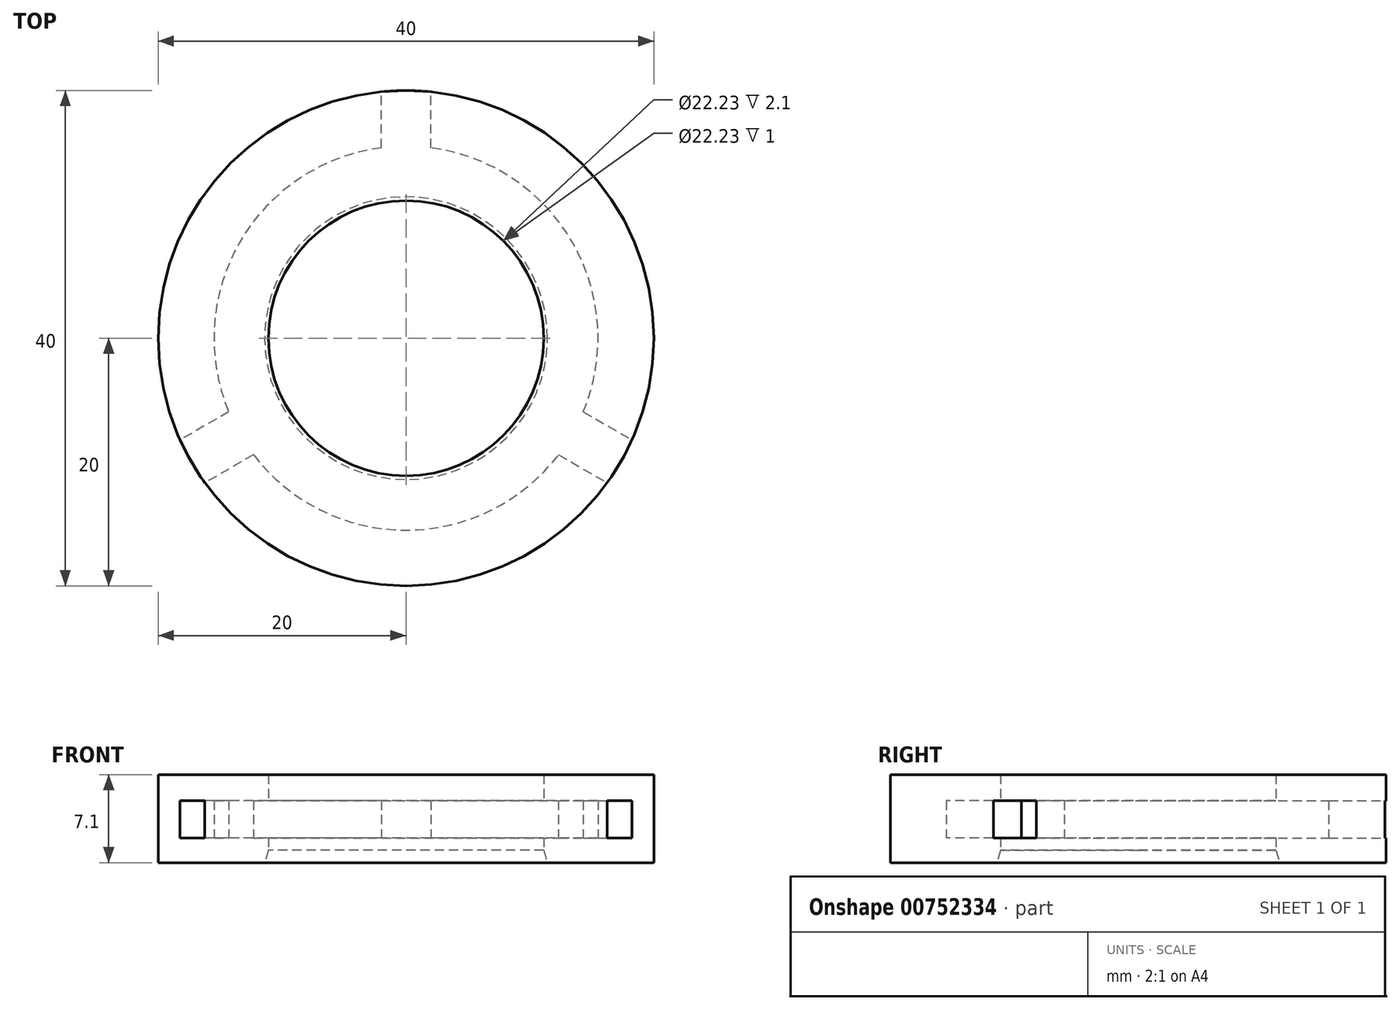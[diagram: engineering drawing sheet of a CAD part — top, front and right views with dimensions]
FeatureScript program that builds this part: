
annotation { "Feature Type Name" : "Feature", "Feature Type Description" : "" }
export const myFeature = defineFeature(function(context is Context, id is Id, definition is map)
    precondition{}
    {
        {
            var Q0;
            Q0=qCreatedBy(makeId("Top.planeOp"),FACE);
            var sketch = newSketch(context, id + "F0", { "sketchPlane" : qUnion([Q0])});
            skCircle(sketch, "E0", {"center": v(0, 0) * mm, "radius": 11.11 * mm});
            skCircle(sketch, "E1", {"center": v(0, 0) * mm, "radius": 20 * mm});
            skSolve(sketch);
        }
        {
            var Q0;
            Q0=qSketchRegion(id+"F0",true);
            extrude(context, id + "F1", {"entities" : qUnion([Q0]), "depth" : 7.1 * mm, "offsetDistance" : 25 * mm});
        }
        {
            var Q0;
            Q0=qCreatedBy(makeId("Top.planeOp"),FACE);
            var sketch = newSketch(context, id + "F2", { "sketchPlane" : qUnion([Q0])});
            skCircle(sketch, "E2", {"center": v(0, 0) * mm, "radius": 11.11 * mm});
            skLineSegment(sketch, "E3.left", {"start": v(-2, 15.37) * mm, "end": v(-2, 19.9) * mm});
            skLineSegment(sketch, "E3.right", {"start": v(2, 15.37) * mm, "end": v(2, 19.9) * mm});
            skLineSegment(sketch, "E4.1.0", {"start": v(-14.31, -5.95) * mm, "end": v(-18.23, -8.22) * mm});
            skLineSegment(sketch, "E4.1.1", {"start": v(-12.31, -9.42) * mm, "end": v(-16.23, -11.68) * mm});
            skLineSegment(sketch, "E4.2.0", {"start": v(12.31, -9.42) * mm, "end": v(16.23, -11.68) * mm});
            skLineSegment(sketch, "E4.2.1", {"start": v(14.31, -5.95) * mm, "end": v(18.23, -8.22) * mm});
            skArc(sketch, "E5", {"start": v(2, 19.9) * mm, "mid": v(0, 20) * mm, "end": v(-2, 19.9) * mm});
            skArc(sketch, "E6", {"start": v(-18.23, -8.22) * mm, "mid": v(-17.32, -10) * mm, "end": v(-16.23, -11.68) * mm});
            skArc(sketch, "E7", {"start": v(16.23, -11.68) * mm, "mid": v(17.32, -10) * mm, "end": v(18.23, -8.22) * mm});
            skArc(sketch, "E8", {"start": v(14.31, -5.95) * mm, "mid": v(13.42, 7.75) * mm, "end": v(2, 15.37) * mm});
            skArc(sketch, "E9", {"start": v(-12.31, -9.42) * mm, "mid": v(0, -15.5) * mm, "end": v(12.31, -9.42) * mm});
            skArc(sketch, "E10", {"start": v(-2, 15.37) * mm, "mid": v(-13.42, 7.75) * mm, "end": v(-14.31, -5.95) * mm});
            skSolve(sketch);
        }
        {
            var Q0;
            Q0 = qSketchRegion(id + "F2", true);
            extrude(context, id + "F3", {"entities" : qUnion([Q0]), "operationType" : NewBodyOperationType.REMOVE, "depth" : 5 * mm, "offsetDistance" : 25 * mm});
        }
        {
            var Q0;
            Q0=qCreatedBy(makeId("Top.planeOp"),FACE);
            var sketch = newSketch(context, id + "F4", { "sketchPlane" : qUnion([Q0])});
            skCircle(sketch, "E11", {"center": v(0, 0) * mm, "radius": 11.11 * mm});
            skLineSegment(sketch, "E12", {"start": v(-2, 15.37) * mm, "end": v(-2, 19.9) * mm});
            skLineSegment(sketch, "E13", {"start": v(2, 15.37) * mm, "end": v(2, 15.37) * mm});
            skLineSegment(sketch, "E14.1.0", {"start": v(-14.31, -5.95) * mm, "end": v(-18.23, -8.22) * mm});
            skLineSegment(sketch, "E14.1.1", {"start": v(-12.31, -9.42) * mm, "end": v(-16.23, -11.68) * mm});
            skLineSegment(sketch, "E14.2.0", {"start": v(12.31, -9.42) * mm, "end": v(16.23, -11.68) * mm});
            skLineSegment(sketch, "E14.2.1", {"start": v(14.31, -5.95) * mm, "end": v(18.23, -8.22) * mm});
            skArc(sketch, "E15", {"start": v(-18.23, -8.22) * mm, "mid": v(-17.32, -10) * mm, "end": v(-16.23, -11.68) * mm});
            skArc(sketch, "E16", {"start": v(-12.31, -9.42) * mm, "mid": v(0, -15.5) * mm, "end": v(12.31, -9.42) * mm});
            skArc(sketch, "E17", {"start": v(-2, 15.37) * mm, "mid": v(-13.42, 7.75) * mm, "end": v(-14.31, -5.95) * mm});
            skLineSegment(sketch, "E18", {"start": v(2, 15.37) * mm, "end": v(2, 19.9) * mm});
            skArc(sketch, "E19", {"start": v(2, 19.9) * mm, "mid": v(0, 20) * mm, "end": v(-2, 19.9) * mm});
            skArc(sketch, "E20", {"start": v(14.31, -5.95) * mm, "mid": v(13.42, 7.75) * mm, "end": v(2, 15.37) * mm});
            skArc(sketch, "E21", {"start": v(16.23, -11.68) * mm, "mid": v(17.32, -10) * mm, "end": v(18.23, -8.22) * mm});
            skSolve(sketch);
        }
        {
            var Q0;
            Q0 = qSketchRegion(id + "F4", true);
            extrude(context, id + "F5", {"entities" : qUnion([Q0]), "operationType" : NewBodyOperationType.ADD, "depth" : 2 * mm, "offsetDistance" : 25 * mm});
        }
        {
            var Q0;
            Q0=makeQuery(id+"F5.opExtrude","CAP_EDGE",EDGE,{"disambiguationData":[OSD([sQuery(id+"F4.wireOp",EDGE,"E11")])],"isStart":true});
            chamfer(context, id + "F6", {"entities" : qUnion([Q0]), "chamferType" : ChamferType.TWO_OFFSETS, "width1" : .3 * mm, "oppositeDirection" : false, "width2" : 1 * mm, "tangentPropagation" : true});
        }
    });
